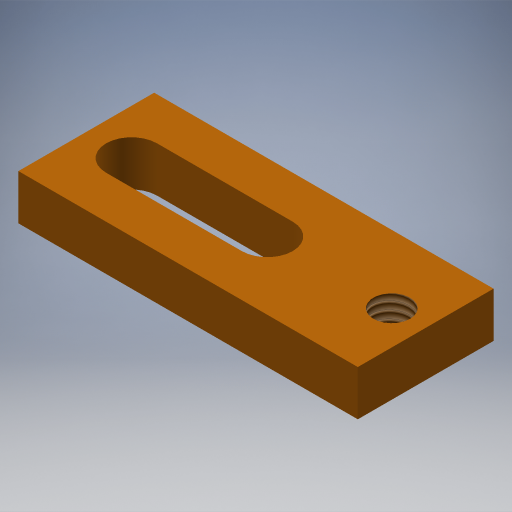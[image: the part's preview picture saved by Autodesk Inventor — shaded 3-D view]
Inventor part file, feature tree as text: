
AUTODESK INVENTOR PART (.ipt)
format: ipt  version: 2024.3 (Build 283343000, 343)  size: 249,344 bytes
history: native  units: mm
features: sketch x3, projected_geometry x3, extrude x2, hole x2
ambient origin geometry x8: Origin, YZ Plane, XZ Plane, XY Plane, X Axis, Y Axis, Z Axis, Center Point
bodies: Volumenkörper1 (feature_tree)
feature tree (10):
  extrude  "Extrusion1"  Depth=30.0mm
  hole  "Bohrung1"  [1 undecoded]
  hole  "Bohrung2"  [1 undecoded]
  extrude  "Extrusion2"  TaperAngle=0.0deg  [1 undecoded]
  sketch  "Skizze2"  dims[d0=12.0mm d1=30.0mm]
  projected_geometry  "Projizierte Kontur1"
  sketch  "Skizze3"  dims[d2=4.0mm d3=0.0mm d5=4.0mm]
  projected_geometry  "Projizierte Kontur2"
  sketch  "Skizze4"  dims[d6=16.0mm d7=4.5mm d8=6.0mm d9=4.0mm d10=2.0mm d11=90.0deg d12=8.0mm d13=20.594885mm d14=3.0mm d15=3.242mm d16=8.0mm d17=4.0mm d18=2.0mm d19=90.0deg d20=8.0mm d21=20.594885mm d22=0.0mm d23=0.0mm]
  projected_geometry  "Projizierte Kontur3"
note: 3 required parameter values undecoded (feature->parameter linkage not recoverable at this tier; creation-order binding heuristic only, values carry confidence <= 0.55)
